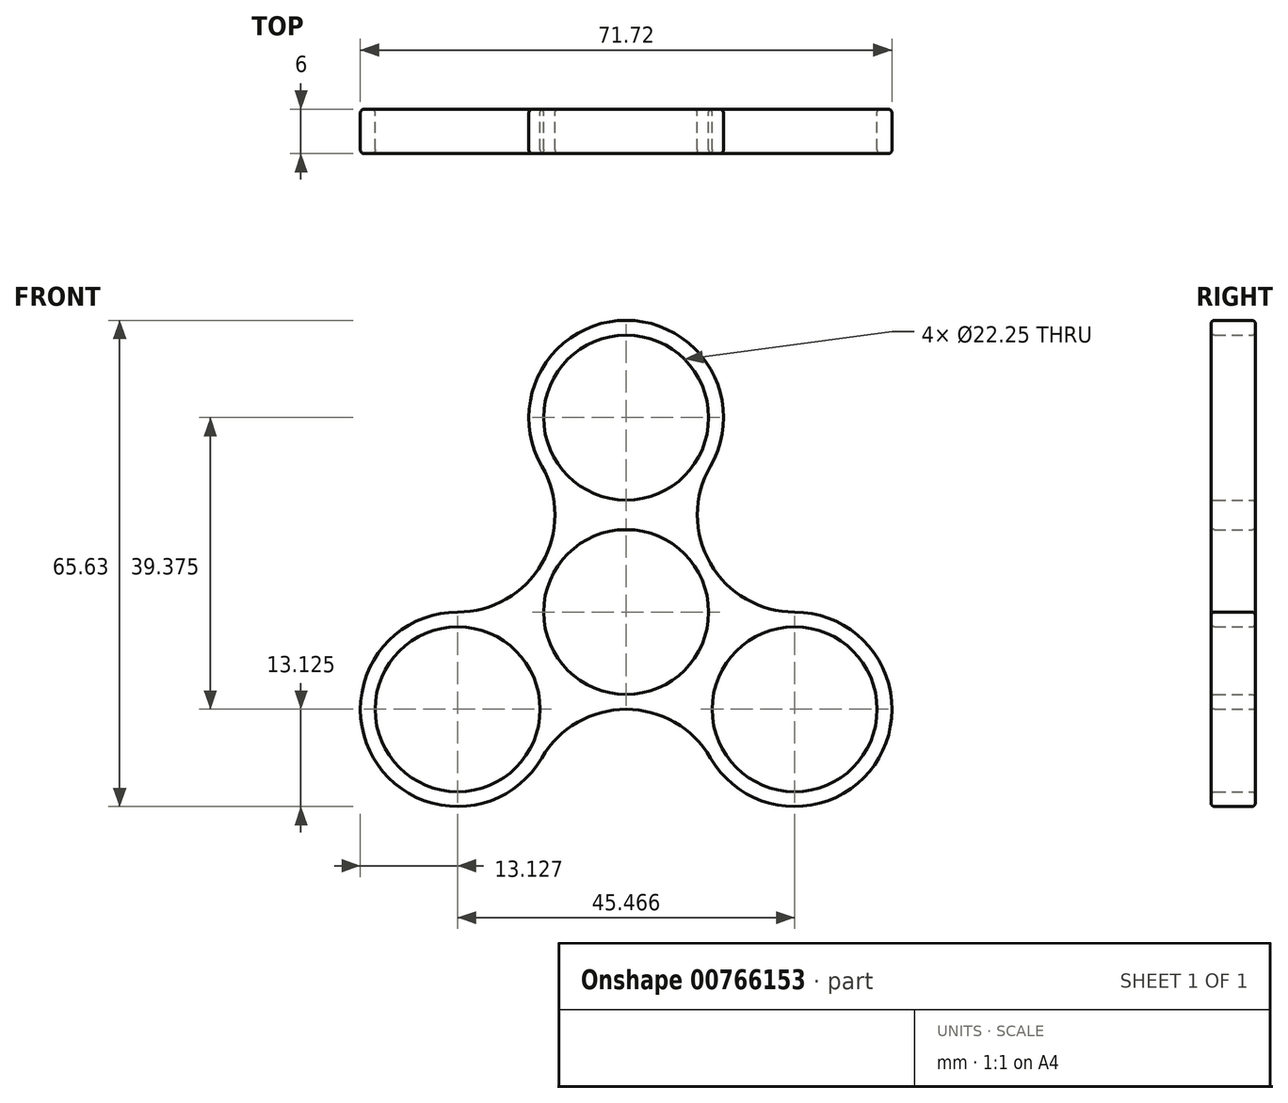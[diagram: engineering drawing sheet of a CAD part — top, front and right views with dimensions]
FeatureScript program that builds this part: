
annotation { "Feature Type Name" : "Feature", "Feature Type Description" : "" }
export const myFeature = defineFeature(function(context is Context, id is Id, definition is map)
    precondition{}
    {
        {
            assignVariable(context, id + "F0", {"name" : "b_height", "anyValue" : 6});
        }
        {
            var Q0;
            Q0=qCreatedBy(makeId("Front.planeOp"),FACE);
            var sketch = newSketch(context, id + "F1", { "sketchPlane" : qUnion([Q0])});
            skCircle(sketch, "E0", {"center": v(0, 0) * mm, "radius": 11.12 * mm});
            skCircle(sketch, "E1", {"center": v(0, 0) * mm, "radius": 13.12 * mm, "construction": true});
            skCircle(sketch, "E2", {"center": v(0, 26.25) * mm, "radius": 11.12 * mm});
            skCircle(sketch, "E3", {"center": v(22.73, -13.12) * mm, "radius": 11.12 * mm});
            skCircle(sketch, "E4", {"center": v(-22.73, -13.12) * mm, "radius": 11.12 * mm});
            skLineSegment(sketch, "E5", {"start": v(0, 26.25) * mm, "end": v(0, 0) * mm, "construction": true});
            skLineSegment(sketch, "E6", {"start": v(0, 0) * mm, "end": v(22.73, -13.12) * mm, "construction": true});
            skLineSegment(sketch, "E7", {"start": v(0, 0) * mm, "end": v(-22.73, -13.12) * mm, "construction": true});
            skLineSegment(sketch, "E8", {"start": v(0, 0) * mm, "end": v(-11.37, 6.56) * mm, "construction": true});
            skLineSegment(sketch, "E9", {"start": v(0, 0) * mm, "end": v(11.37, 6.56) * mm, "construction": true});
            skLineSegment(sketch, "E10", {"start": v(0, 0) * mm, "end": v(0, -13.12) * mm, "construction": true});
            skLineSegment(sketch, "E11", {"start": v(0, 26.25) * mm, "end": v(-11.37, 19.69) * mm, "construction": true});
            skLineSegment(sketch, "E12", {"start": v(-22.73, -13.12) * mm, "end": v(-22.73, 0) * mm, "construction": true});
            skArc(sketch, "E13", {"start": v(-22.73, 0) * mm, "mid": v(-11.37, 6.56) * mm, "end": v(-11.37, 19.69) * mm});
            skLineSegment(sketch, "E14", {"start": v(0, 26.25) * mm, "end": v(11.37, 19.69) * mm, "construction": true});
            skLineSegment(sketch, "E15", {"start": v(22.73, -13.12) * mm, "end": v(22.73, 0) * mm, "construction": true});
            skLineSegment(sketch, "E16", {"start": v(22.73, -13.12) * mm, "end": v(11.37, -19.69) * mm, "construction": true});
            skLineSegment(sketch, "E17", {"start": v(-22.73, -13.12) * mm, "end": v(-11.37, -19.69) * mm, "construction": true});
            skLineSegment(sketch, "E18", {"start": v(11.37, 19.69) * mm, "end": v(11.37, 19.69) * mm});
            skArc(sketch, "E19", {"start": v(11.37, -19.69) * mm, "mid": v(0, -13.13) * mm, "end": v(-11.37, -19.69) * mm});
            skLineSegment(sketch, "E20", {"start": v(-22.73, 0) * mm, "end": v(-22.73, 0) * mm});
            skLineSegment(sketch, "E21", {"start": v(-11.37, -19.69) * mm, "end": v(-11.37, -19.69) * mm});
            skArc(sketch, "E22", {"start": v(-22.73, 0) * mm, "mid": v(-34.1, -19.69) * mm, "end": v(-11.37, -19.69) * mm});
            skArc(sketch, "E23", {"start": v(-11.37, -19.69) * mm, "mid": v(-11.37, -6.56) * mm, "end": v(-22.73, 0) * mm, "construction": true});
            skArc(sketch, "E24", {"start": v(22.73, 0) * mm, "mid": v(11.37, -6.56) * mm, "end": v(11.37, -19.69) * mm, "construction": true});
            skArc(sketch, "E25", {"start": v(11.37, -19.69) * mm, "mid": v(34.1, -19.69) * mm, "end": v(22.73, 0) * mm});
            skLineSegment(sketch, "E26", {"start": v(-11.37, 19.69) * mm, "end": v(-11.37, 19.69) * mm});
            skArc(sketch, "E27", {"start": v(11.37, 19.69) * mm, "mid": v(11.37, 6.56) * mm, "end": v(22.73, 0) * mm});
            skArc(sketch, "E28", {"start": v(11.37, 19.69) * mm, "mid": v(0, 39.38) * mm, "end": v(-11.37, 19.69) * mm});
            skArc(sketch, "E29", {"start": v(-11.37, 19.69) * mm, "mid": v(0, 13.12) * mm, "end": v(11.37, 19.69) * mm, "construction": true});
            skSolve(sketch);
        }
        {
            var Q0;
            {var subQ0=sQuery(id+"F1.wireOp",EDGE,"E13");var subQ1=sQuery(id+"F1.wireOp",EDGE,"E1");var subQ2=makeQuery(id+"F1.imprint","INTERSECT",VERTEX,{"derivedFrom":[subQ1,subQ0]});Q0=makeQuery(id+"F1.imprint","IMPRINT",FACE,{"disambiguationData":[TD([[makeQuery(id+"F1.imprint","IMPRINT",EDGE,{"disambiguationData":[TD([[subQ2,1.0]])],"derivedFrom":subQ1}),-1.0]])]});}
            var Q1;
            Q1=makeQuery(id+"F1.imprint","IMPRINT",FACE,{"disambiguationData":[TD([[makeQuery(id+"F1.imprint","IMPRINT",EDGE,{"derivedFrom":sQuery(id+"F1.wireOp",EDGE,"E0")}),-1.0]])]});
            var Q2;
            {var subQ0=sQuery(id+"F1.wireOp",EDGE,"E13");var subQ1=sQuery(id+"F1.wireOp",EDGE,"E1");var subQ2=makeQuery(id+"F1.imprint","INTERSECT",VERTEX,{"derivedFrom":[subQ1,subQ0]});Q2=makeQuery(id+"F1.imprint","IMPRINT",FACE,{"disambiguationData":[TD([[makeQuery(id+"F1.imprint","IMPRINT",EDGE,{"disambiguationData":[TD([[subQ2,-1.0]])],"derivedFrom":subQ1}),-1.0]])]});}
            var Q3;
            Q3=makeQuery(id+"F1.imprint","IMPRINT",FACE,{"disambiguationData":[TD([[makeQuery(id+"F1.imprint","IMPRINT",EDGE,{"derivedFrom":sQuery(id+"F1.wireOp",EDGE,"E4")}),-1.0]])]});
            var Q4;
            {var subQ0=sQuery(id+"F1.wireOp",EDGE,"E19");var subQ1=sQuery(id+"F1.wireOp",EDGE,"E1");var subQ2=makeQuery(id+"F1.imprint","INTERSECT",VERTEX,{"derivedFrom":[subQ1,subQ0]});Q4=makeQuery(id+"F1.imprint","IMPRINT",FACE,{"disambiguationData":[TD([[makeQuery(id+"F1.imprint","IMPRINT",EDGE,{"disambiguationData":[TD([[subQ2,1.0]])],"derivedFrom":subQ1}),-1.0]])]});}
            var Q5;
            {var subQ0=sQuery(id+"F1.wireOp",EDGE,"E19");var subQ1=sQuery(id+"F1.wireOp",EDGE,"E1");var subQ2=makeQuery(id+"F1.imprint","INTERSECT",VERTEX,{"derivedFrom":[subQ1,subQ0]});Q5=makeQuery(id+"F1.imprint","IMPRINT",FACE,{"disambiguationData":[TD([[makeQuery(id+"F1.imprint","IMPRINT",EDGE,{"disambiguationData":[TD([[subQ2,-1.0]])],"derivedFrom":subQ1}),-1.0]])]});}
            var Q6;
            {var subQ0=sQuery(id+"F1.wireOp",EDGE,"E18");var subQ1=sQuery(id+"F1.wireOp",EDGE,"E1");var subQ2=makeQuery(id+"F1.imprint","INTERSECT",VERTEX,{"derivedFrom":[subQ1,subQ0]});Q6=makeQuery(id+"F1.imprint","IMPRINT",FACE,{"disambiguationData":[TD([[makeQuery(id+"F1.imprint","IMPRINT",EDGE,{"disambiguationData":[TD([[subQ2,1.0]])],"derivedFrom":subQ1}),-1.0]])]});}
            var Q7;
            Q7=makeQuery(id+"F1.imprint","IMPRINT",FACE,{"disambiguationData":[TD([[makeQuery(id+"F1.imprint","IMPRINT",EDGE,{"derivedFrom":sQuery(id+"F1.wireOp",EDGE,"E3")}),-1.0]])]});
            var Q8;
            {var subQ0=sQuery(id+"F1.wireOp",EDGE,"E18");var subQ1=sQuery(id+"F1.wireOp",EDGE,"E1");var subQ2=makeQuery(id+"F1.imprint","INTERSECT",VERTEX,{"derivedFrom":[subQ1,subQ0]});Q8=makeQuery(id+"F1.imprint","IMPRINT",FACE,{"disambiguationData":[TD([[makeQuery(id+"F1.imprint","IMPRINT",EDGE,{"disambiguationData":[TD([[subQ2,-1.0]])],"derivedFrom":subQ1}),-1.0]])]});}
            var Q9;
            Q9=makeQuery(id+"F1.imprint","IMPRINT",FACE,{"disambiguationData":[TD([[makeQuery(id+"F1.imprint","IMPRINT",EDGE,{"derivedFrom":sQuery(id+"F1.wireOp",EDGE,"E2")}),-1.0]])]});
            extrude(context, id + "F2", {"entities" : qUnion([Q0, Q1, Q2, Q3, Q4, Q5, Q6, Q7, Q8, Q9]), "depth" : (getVariable(context, 'b_height')) * mm, "offsetDistance" : 25 * mm});
        }
        {
            var Q0;
            Q0=makeQuery(id+"F2.opExtrude","CAP_FACE",FACE,{"disambiguationData":[OSD([sQuery(id+"F1.wireOp",EDGE,"E0"),sQuery(id+"F1.wireOp",EDGE,"E2"),sQuery(id+"F1.wireOp",EDGE,"E3"),sQuery(id+"F1.wireOp",EDGE,"E4"),sQuery(id+"F1.wireOp",EDGE,"E13"),sQuery(id+"F1.wireOp",EDGE,"E19"),sQuery(id+"F1.wireOp",EDGE,"E22"),sQuery(id+"F1.wireOp",EDGE,"E25"),sQuery(id+"F1.wireOp",EDGE,"E27"),sQuery(id+"F1.wireOp",EDGE,"E28")])],"isStart":false});
            var Q1;
            Q1=makeQuery(id+"F2.opExtrude","CAP_FACE",FACE,{"disambiguationData":[OSD([sQuery(id+"F1.wireOp",EDGE,"E0"),sQuery(id+"F1.wireOp",EDGE,"E2"),sQuery(id+"F1.wireOp",EDGE,"E3"),sQuery(id+"F1.wireOp",EDGE,"E4"),sQuery(id+"F1.wireOp",EDGE,"E13"),sQuery(id+"F1.wireOp",EDGE,"E19"),sQuery(id+"F1.wireOp",EDGE,"E22"),sQuery(id+"F1.wireOp",EDGE,"E25"),sQuery(id+"F1.wireOp",EDGE,"E27"),sQuery(id+"F1.wireOp",EDGE,"E28")])],"isStart":true});
            fillet(context, id + "F3", {"entities" : qUnion([Q0, Q1]), "radius" : 0.5 * mm, "tangentPropagation" : true, "allowEdgeOverflow" : false});
        }
    });
